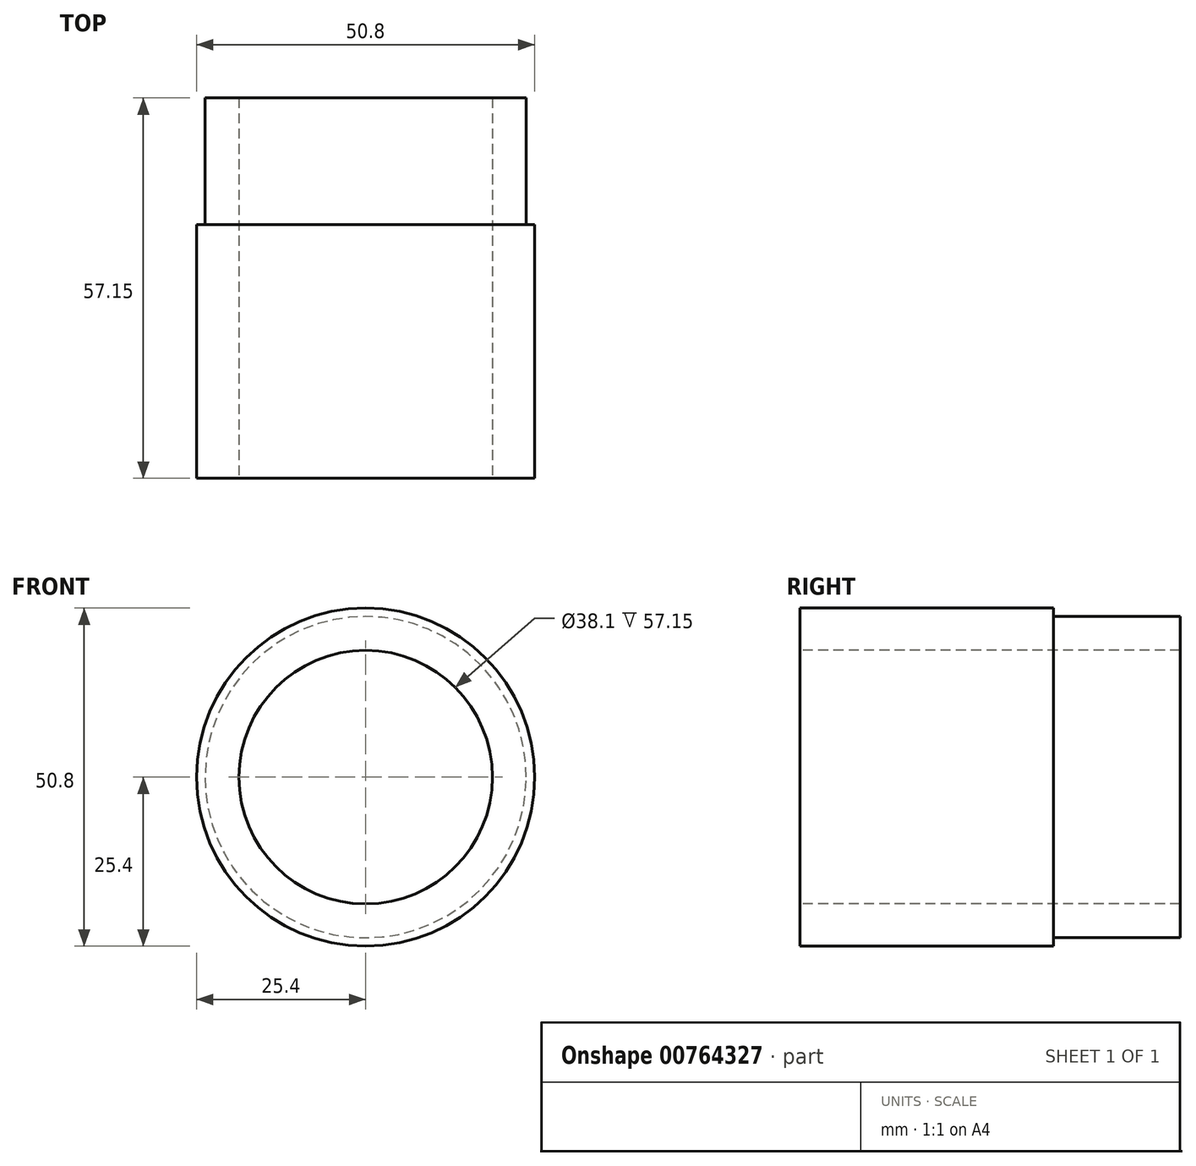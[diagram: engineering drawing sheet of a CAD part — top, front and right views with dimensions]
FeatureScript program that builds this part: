
annotation { "Feature Type Name" : "Feature", "Feature Type Description" : "" }
export const myFeature = defineFeature(function(context is Context, id is Id, definition is map)
    precondition{}
    {
        {
            var Q0;
            Q0=qCreatedBy(makeId("Front.planeOp"),FACE);
            var sketch = newSketch(context, id + "F0", { "sketchPlane" : qUnion([Q0])});
            skCircle(sketch, "E0", {"center": v(0, 0) * mm, "radius": 24.13 * mm});
            skSolve(sketch);
        }
        {
            var Q0;
            Q0=qSketchRegion(id+"F0",true);
            extrude(context, id + "F1", {"entities" : qUnion([Q0]), "oppositeDirection" : true, "depth" : 19.05 * mm});
        }
        {
            var Q0;
            Q0=makeQuery(id+"F1.opExtrude","CAP_FACE",FACE,{"disambiguationData":[OSD([sQuery(id+"F0.wireOp",EDGE,"E0")])],"isStart":true});
            var sketch = newSketch(context, id + "F2", { "sketchPlane" : qUnion([Q0])});
            skCircle(sketch, "E1", {"center": v(0, 0) * mm, "radius": 25.4 * mm});
            skSolve(sketch);
        }
        {
            var Q0;
            Q0=qSketchRegion(id+"F2",true);
            extrude(context, id + "F3", {"entities" : qUnion([Q0]), "operationType" : NewBodyOperationType.ADD, "depth" : 38.1 * mm});
        }
        {
            var Q0;
            Q0=makeQuery(id+"F3.opExtrude","CAP_FACE",FACE,{"disambiguationData":[OSD([sQuery(id+"F2.wireOp",EDGE,"E1")])],"isStart":false});
            var sketch = newSketch(context, id + "F4", { "sketchPlane" : qUnion([Q0])});
            skCircle(sketch, "E2", {"center": v(0, 0) * mm, "radius": 19.05 * mm});
            skSolve(sketch);
        }
        {
            var Q0;
            Q0=qSketchRegion(id+"F4",true);
            extrude(context, id + "F5", {"entities" : qUnion([Q0]), "operationType" : NewBodyOperationType.REMOVE, "endBound" : BoundingType.THROUGH_ALL, "oppositeDirection" : true, "depth" : 25.4 * mm});
        }
    });
